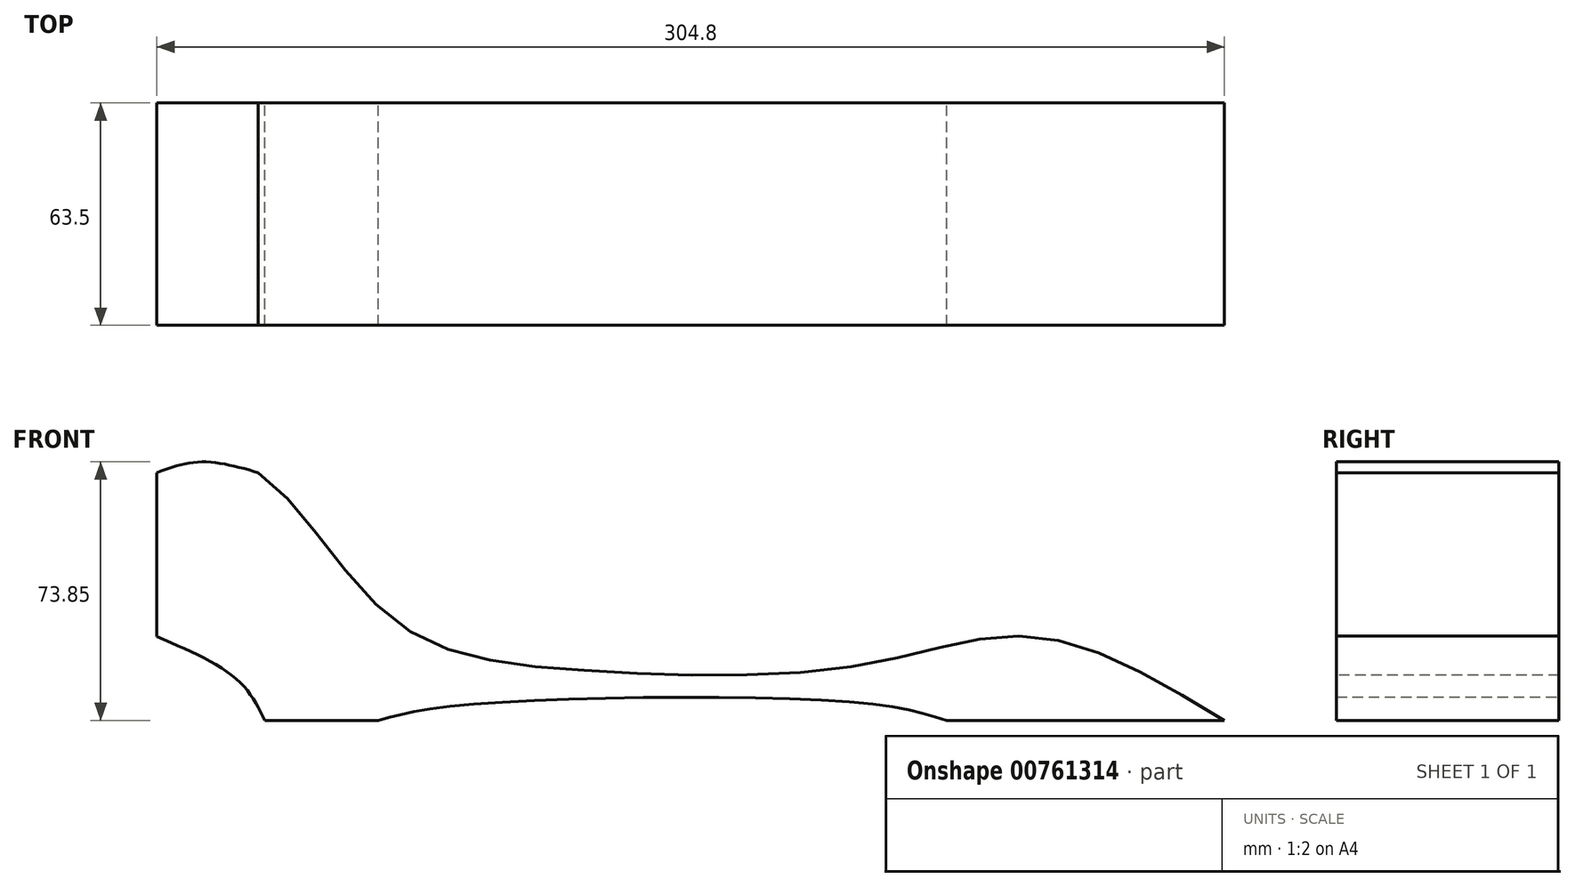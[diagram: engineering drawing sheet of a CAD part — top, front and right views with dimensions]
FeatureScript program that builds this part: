
annotation { "Feature Type Name" : "Feature", "Feature Type Description" : "" }
export const myFeature = defineFeature(function(context is Context, id is Id, definition is map)
    precondition{}
    {
        {
            var Q0;
            Q0=qCreatedBy(makeId("Front.planeOp"),FACE);
            var sketch = newSketch(context, id + "F0", { "sketchPlane" : qUnion([Q0])});
            skLineSegment(sketch, "E0", {"start": v(327.6, -23.92) * mm, "end": v(248.3, -23.92) * mm});
            skLineSegment(sketch, "E1", {"start": v(22.8, 0) * mm, "end": v(22.8, 46.85) * mm});
            skFitSpline(sketch, "E2", {"points": [v(22.8, 52.28) * mm, v(51.78, 46.85) * mm, v(89.78, 5.33) * mm, v(143.08, -9.5) * mm, v(224.2, -8.1) * mm, v(273.8, 0) * mm, v(327.6, -23.92) * mm], "startDerivative": vector(242.38, 9.85) * mm, "endDerivative": vector(316.6, -191.63) * mm});
            skFitSpline(sketch, "E3", {"points": [v(86.07, -23.92) * mm, v(108.78, -19.7) * mm, v(222.35, -18.77) * mm, v(248.3, -23.92) * mm], "startDerivative": vector(69.03, 19.64) * mm, "endDerivative": vector(74.93, -23.72) * mm});
            skFitSpline(sketch, "E4", {"points": [v(53.62, -23.92) * mm, v(45.74, -12.28) * mm, v(22.8, 0) * mm], "startDerivative": vector(-14.11, 28.78) * mm, "endDerivative": vector(-45.9, 19.53) * mm});
            skFitSpline(sketch, "E5", {"points": [v(51.78, 46.85) * mm, v(35.37, 49.92) * mm, v(22.8, 46.85) * mm], "startDerivative": vector(-31.93, 9.07) * mm, "endDerivative": vector(-25.9, -9.47) * mm});
            skLineSegment(sketch, "E6.trimOffspring", {"start": v(86.07, -23.92) * mm, "end": v(53.62, -23.92) * mm});
            skSolve(sketch);
        }
        {
            var Q0;
            Q0=makeQuery(id+"F0.imprint","IMPRINT",FACE,{"disambiguationData":[TD([[makeQuery(id+"F0.imprint","IMPRINT",EDGE,{"derivedFrom":sQuery(id+"F0.wireOp",EDGE,"E0")}),-1.0]])]});
            extrude(context, id + "F1", {"entities" : qUnion([Q0]), "depth" : 63.5 * mm, "offsetDistance" : 25.4 * mm});
        }
    });
